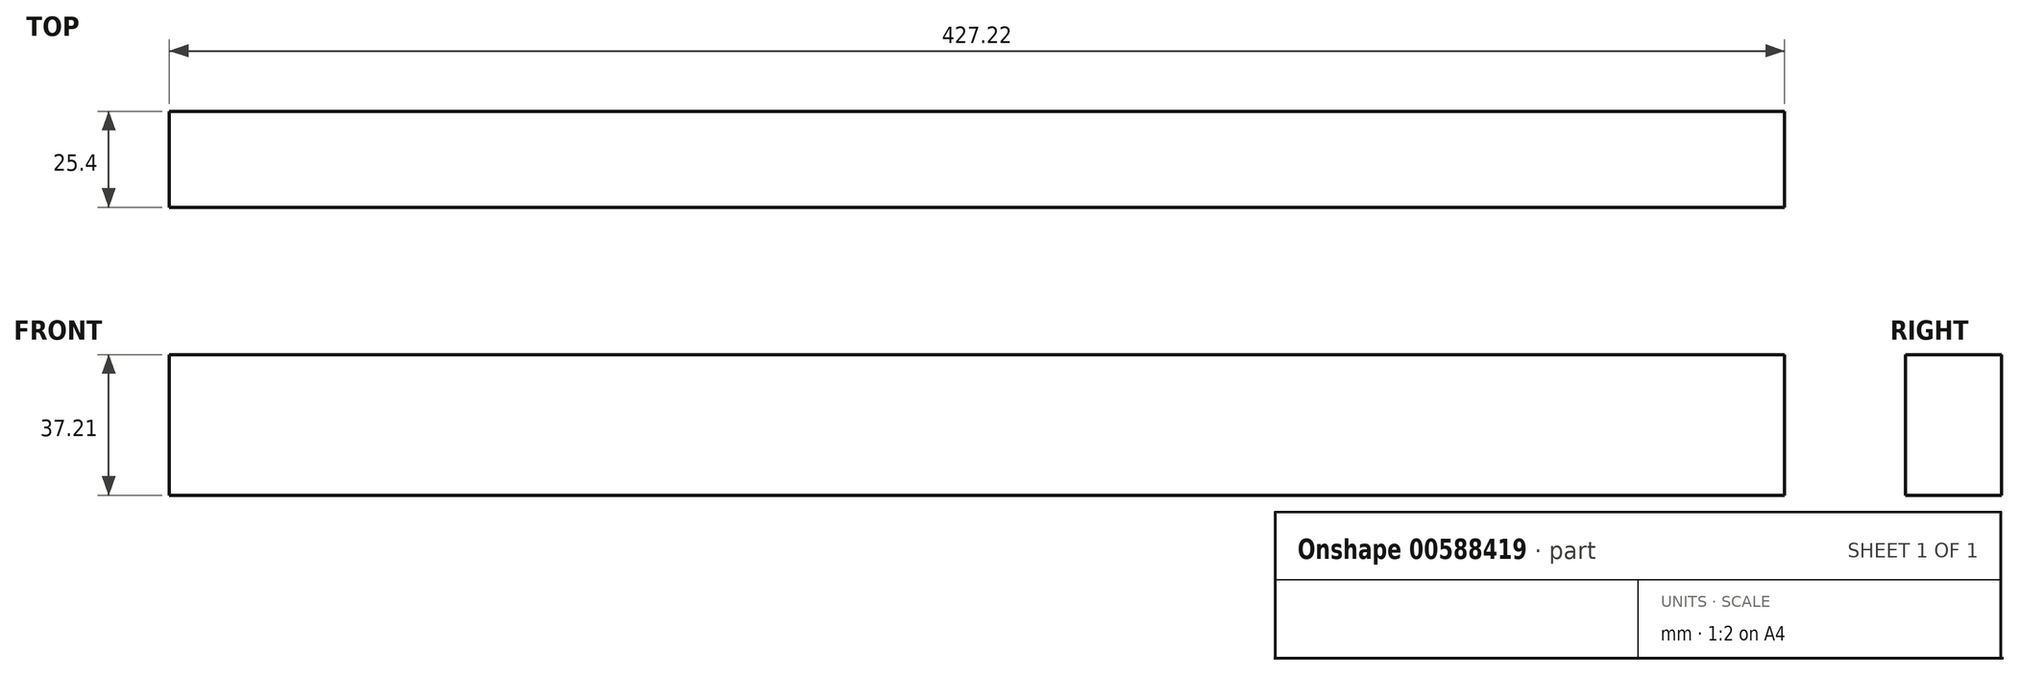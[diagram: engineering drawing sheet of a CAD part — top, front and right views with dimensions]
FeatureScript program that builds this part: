
annotation { "Feature Type Name" : "Feature", "Feature Type Description" : "" }
export const myFeature = defineFeature(function(context is Context, id is Id, definition is map)
    precondition{}
    {
        {
            var Q0;
            Q0=qCreatedBy(makeId("Front.planeOp"),FACE);
            var sketch = newSketch(context, id + "F0", { "sketchPlane" : qUnion([Q0])});
            skLineSegment(sketch, "E0.bottom", {"start": v(-125.95, 61.6) * mm, "end": v(301.27, 61.6) * mm});
            skLineSegment(sketch, "E0.top", {"start": v(-125.95, 24.4) * mm, "end": v(301.27, 24.4) * mm});
            skLineSegment(sketch, "E0.left", {"start": v(-125.95, 61.6) * mm, "end": v(-125.95, 24.4) * mm});
            skLineSegment(sketch, "E0.right", {"start": v(301.27, 61.6) * mm, "end": v(301.27, 24.4) * mm});
            skSolve(sketch);
        }
        {
            var Q0;
            Q0 = qSketchRegion(id + "F0", true);
            extrude(context, id + "F1", {"entities" : qUnion([Q0]), "endBound" : BoundingType.SYMMETRIC, "depth" : 25.4 * mm, "offsetDistance" : 25.4 * mm});
        }
    });
